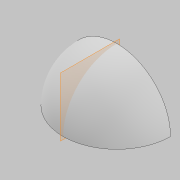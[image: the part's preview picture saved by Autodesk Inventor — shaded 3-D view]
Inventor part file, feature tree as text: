
AUTODESK INVENTOR PART (.ipt)
format: ipt  version: 2021 (Build 250183000, 183)  size: 119,808 bytes
history: native  units: mm
features: other x3, revolve x1, sketch x1
ambient origin geometry x8: Origin, YZ Plane, XZ Plane, XY Plane, X Axis, Y Axis, Z Axis, Center Point
bodies: Body1 (feature_tree)
feature tree (5):
  revolve  "Revolution1"  [1 undecoded]
  other  "midPlane"
  sketch  "Sketch1"  dims[d0=10.0mm d1=900.0mm d2=0.0mm d3=0.0mm d6=180.0deg d7=900.0mm d8=-900.0mm]
  other  "tangent1"
  other  "tangent2"
note: 1 required parameter value undecoded (feature->parameter linkage not recoverable at this tier; creation-order binding heuristic only, values carry confidence <= 0.55)
